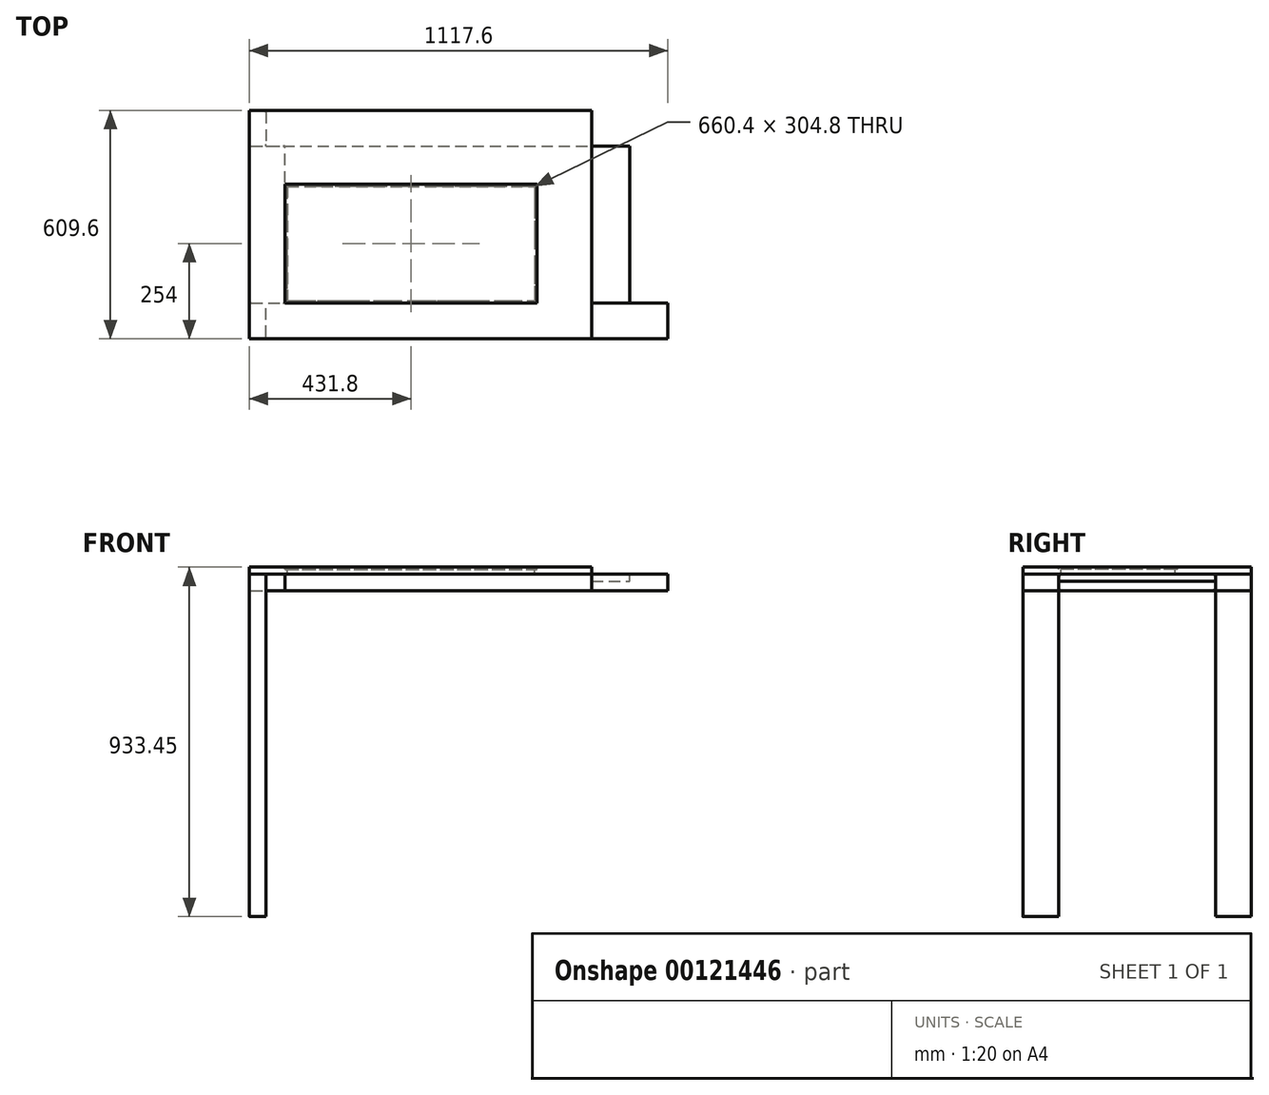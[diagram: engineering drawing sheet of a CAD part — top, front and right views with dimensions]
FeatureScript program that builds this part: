
annotation { "Feature Type Name" : "Feature", "Feature Type Description" : "" }
export const myFeature = defineFeature(function(context is Context, id is Id, definition is map)
    precondition{}
    {
        {
            var Q0;
            Q0=qCreatedBy(makeId("Top.planeOp"),FACE);
            var sketch = newSketch(context, id + "F0", { "sketchPlane" : qUnion([Q0])});
            skLineSegment(sketch, "E0.bottom", {"start": v(457.2, 304.8) * mm, "end": v(-457.2, 304.8) * mm});
            skLineSegment(sketch, "E0.top", {"start": v(457.2, -304.8) * mm, "end": v(-457.2, -304.8) * mm});
            skLineSegment(sketch, "E0.left", {"start": v(457.2, 304.8) * mm, "end": v(457.2, -304.8) * mm});
            skLineSegment(sketch, "E0.right", {"start": v(-457.2, 304.8) * mm, "end": v(-457.2, -304.8) * mm});
            skPoint(sketch, "E0.middle", {"position": v(0, 0) * mm});
            skSolve(sketch);
        }
        {
            var Q0;
            Q0 = qSketchRegion(id + "F0", true);
            extrude(context, id + "F1", {"entities" : qUnion([Q0]), "depth" : 19.05 * mm});
        }
        {
            var Q0;
            Q0=makeQuery(id+"F1.opExtrude","CAP_FACE",FACE,{"disambiguationData":[OSD([sQuery(id+"F0.wireOp",EDGE,"E0.bottom"),sQuery(id+"F0.wireOp",EDGE,"E0.top"),sQuery(id+"F0.wireOp",EDGE,"E0.left"),sQuery(id+"F0.wireOp",EDGE,"E0.right")])],"isStart":true});
            var sketch = newSketch(context, id + "F2", { "sketchPlane" : qUnion([Q0])});
            skLineSegment(sketch, "E1.bottom", {"start": v(-457.2, 304.8) * mm, "end": v(-412.75, 304.8) * mm});
            skLineSegment(sketch, "E1.top", {"start": v(-457.2, 209.55) * mm, "end": v(-412.75, 209.55) * mm});
            skLineSegment(sketch, "E1.left", {"start": v(-457.2, 304.8) * mm, "end": v(-457.2, 209.55) * mm});
            skLineSegment(sketch, "E1.right", {"start": v(-412.75, 304.8) * mm, "end": v(-412.75, 209.55) * mm});
            skLineSegment(sketch, "E2.bottom", {"start": v(-457.2, -304.8) * mm, "end": v(-412.75, -304.8) * mm});
            skLineSegment(sketch, "E2.top", {"start": v(-457.2, -209.55) * mm, "end": v(-412.75, -209.55) * mm});
            skLineSegment(sketch, "E2.left", {"start": v(-457.2, -304.8) * mm, "end": v(-457.2, -209.55) * mm});
            skLineSegment(sketch, "E2.right", {"start": v(-412.75, -304.8) * mm, "end": v(-412.75, -209.55) * mm});
            skLineSegment(sketch, "E3.bottom", {"start": v(-412.75, -209.55) * mm, "end": v(457.2, -209.55) * mm});
            skLineSegment(sketch, "E3.top", {"start": v(-412.75, -304.8) * mm, "end": v(457.2, -304.8) * mm});
            skLineSegment(sketch, "E3.left", {"start": v(-412.75, -209.55) * mm, "end": v(-412.75, -304.8) * mm});
            skLineSegment(sketch, "E3.right", {"start": v(457.2, -209.55) * mm, "end": v(457.2, -304.8) * mm});
            skLineSegment(sketch, "E4.bottom", {"start": v(-412.75, 209.55) * mm, "end": v(660.4, 209.55) * mm});
            skLineSegment(sketch, "E4.top", {"start": v(-412.75, 304.8) * mm, "end": v(660.4, 304.8) * mm});
            skLineSegment(sketch, "E4.left", {"start": v(-412.75, 209.55) * mm, "end": v(-412.75, 304.8) * mm});
            skLineSegment(sketch, "E4.right", {"start": v(660.4, 209.55) * mm, "end": v(660.4, 304.8) * mm});
            skLineSegment(sketch, "E5.bottom", {"start": v(-457.2, 209.55) * mm, "end": v(-361.95, 209.55) * mm});
            skLineSegment(sketch, "E5.top", {"start": v(-457.2, -209.55) * mm, "end": v(-361.95, -209.55) * mm});
            skLineSegment(sketch, "E5.left", {"start": v(-457.2, 209.55) * mm, "end": v(-457.2, -209.55) * mm});
            skLineSegment(sketch, "E5.right", {"start": v(-361.95, 209.55) * mm, "end": v(-361.95, -209.55) * mm});
            skLineSegment(sketch, "E6.bottom", {"start": v(355.6, -209.55) * mm, "end": v(558.8, -209.55) * mm});
            skLineSegment(sketch, "E6.top", {"start": v(355.6, 209.55) * mm, "end": v(558.8, 209.55) * mm});
            skLineSegment(sketch, "E6.left", {"start": v(355.6, -209.55) * mm, "end": v(355.6, 209.55) * mm});
            skLineSegment(sketch, "E6.right", {"start": v(558.8, -209.55) * mm, "end": v(558.8, 209.55) * mm});
            skSolve(sketch);
        }
        {
            var Q0;
            {var subQ3=sQuery(id+"F2.wireOp",EDGE,"E4.left");Q0=makeQuery(id+"F2.imprint","IMPRINT",FACE,{"disambiguationData":[TD([[makeQuery(id+"F2.imprint","IMPRINT",EDGE,{"derivedFrom":subQ3}),-1.0]])]});}
            var Q1;
            {var subQ1=sQuery(id+"F2.wireOp",EDGE,"E3.bottom");Q1=makeQuery(id+"F2.imprint","IMPRINT",FACE,{"disambiguationData":[TD([[makeQuery(id+"F2.imprint","IMPRINT",EDGE,{"derivedFrom":subQ1}),-1.0]])]});}
            var Q2;
            {var subQ0=sQuery(id+"F2.wireOp",EDGE,"E4.right");Q2=makeQuery(id+"F2.imprint","IMPRINT",FACE,{"disambiguationData":[TD([[makeQuery(id+"F2.imprint","IMPRINT",EDGE,{"derivedFrom":subQ0}),1.0]])]});}
            extrude(context, id + "F3", {"entities" : qUnion([Q0, Q1, Q2]), "depth" : 44.45 * mm});
        }
        {
            var Q0;
            {var subQ5=sQuery(id+"F2.wireOp",EDGE,"E5.left");Q0=makeQuery(id+"F2.imprint","IMPRINT",FACE,{"disambiguationData":[TD([[makeQuery(id+"F2.imprint","IMPRINT",EDGE,{"derivedFrom":subQ5}),-1.0]])]});}
            extrude(context, id + "F4", {"entities" : qUnion([Q0]), "depth" : 44.45 * mm});
        }
        {
            var Q0;
            Q0=makeQuery(id+"F2.imprint","IMPRINT",FACE,{"disambiguationData":[TD([[makeQuery(id+"F2.imprint","IMPRINT",EDGE,{"derivedFrom":sQuery(id+"F2.wireOp",EDGE,"E6.bottom")}),1.0]])]});
            extrude(context, id + "F5", {"entities" : qUnion([Q0]), "depth" : 19.05 * mm});
        }
        {
            var Q0;
            Q0=makeQuery(id+"F2.imprint","IMPRINT",FACE,{"disambiguationData":[TD([[makeQuery(id+"F2.imprint","IMPRINT",EDGE,{"derivedFrom":sQuery(id+"F2.wireOp",EDGE,"E1.bottom")}),1.0]])]});
            var Q1;
            Q1=makeQuery(id+"F2.imprint","IMPRINT",FACE,{"disambiguationData":[TD([[makeQuery(id+"F2.imprint","IMPRINT",EDGE,{"derivedFrom":sQuery(id+"F2.wireOp",EDGE,"E2.bottom")}),-1.0]])]});
            extrude(context, id + "F6", {"entities" : qUnion([Q0, Q1]), "depth" : 914.4 * mm});
        }
        {
            var Q0;
            Q0=makeQuery(id+"F6.opExtrude","SWEPT_EDGE",EDGE,{"disambiguationData":[OSD([sQuery(id+"F2.wireOp",EDGE,"E1.left"),sQuery(id+"F2.wireOp",EDGE,"E5.bottom"),sQuery(id+"F2.wireOp",EDGE,"E5.left")])]});
            var Q1;
            Q1=makeQuery(id+"F6.opExtrude","SWEPT_EDGE",EDGE,{"disambiguationData":[OSD([sQuery(id+"F2.wireOp",EDGE,"E4.left"),sQuery(id+"F2.wireOp",EDGE,"E5.bottom")])]});
            var Q2;
            Q2=makeQuery(id+"F6.opExtrude","SWEPT_EDGE",EDGE,{"disambiguationData":[OSD([sQuery(id+"F2.wireOp",EDGE,"E1.bottom"),sQuery(id+"F2.wireOp",EDGE,"E4.top"),sQuery(id+"F2.wireOp",EDGE,"E4.left")])]});
            var Q3;
            Q3=makeQuery(id+"F3.opExtrude","CAP_EDGE",EDGE,{"disambiguationData":[OSD([sQuery(id+"F2.wireOp",EDGE,"E4.top")])],"isStart":false});
            var Q4;
            Q4=makeQuery(id+"F3.opExtrude","CAP_EDGE",EDGE,{"disambiguationData":[OSD([sQuery(id+"F2.wireOp",EDGE,"E4.bottom"),sQuery(id+"F2.wireOp",EDGE,"E5.bottom")])],"isStart":false});
            var Q5;
            Q5=makeQuery(id+"F3.opExtrude","CAP_EDGE",EDGE,{"disambiguationData":[OSD([sQuery(id+"F2.wireOp",EDGE,"E4.bottom"),sQuery(id+"F2.wireOp",EDGE,"E5.bottom")])],"isStart":true});
            var Q6;
            Q6=makeQuery(id+"F4.opExtrude","CAP_EDGE",EDGE,{"disambiguationData":[OSD([sQuery(id+"F2.wireOp",EDGE,"E5.left")])],"isStart":false});
            var Q7;
            Q7=makeQuery(id+"F4.opExtrude","CAP_EDGE",EDGE,{"disambiguationData":[OSD([sQuery(id+"F2.wireOp",EDGE,"E5.right")])],"isStart":false});
            var Q8;
            Q8=makeQuery(id+"F4.opExtrude","CAP_EDGE",EDGE,{"disambiguationData":[OSD([sQuery(id+"F2.wireOp",EDGE,"E5.right")])],"isStart":true});
            var Q9;
            Q9=makeQuery(id+"F3.opExtrude","CAP_EDGE",EDGE,{"disambiguationData":[OSD([sQuery(id+"F2.wireOp",EDGE,"E3.top")])],"isStart":true});
            var Q10;
            Q10=makeQuery(id+"F3.opExtrude","CAP_EDGE",EDGE,{"disambiguationData":[OSD([sQuery(id+"F2.wireOp",EDGE,"E3.top")])],"isStart":false});
            var Q11;
            Q11=makeQuery(id+"F3.opExtrude","CAP_EDGE",EDGE,{"disambiguationData":[OSD([sQuery(id+"F2.wireOp",EDGE,"E3.bottom"),sQuery(id+"F2.wireOp",EDGE,"E5.top"),sQuery(id+"F2.wireOp",EDGE,"E6.bottom"),sQuery(id+"F2.wireOp",EDGE,"GO6ybiZl-LZOK-cMtS-mfAd-nQg24DWnIChV")])],"isStart":false});
            var Q12;
            Q12=makeQuery(id+"F6.opExtrude","SWEPT_EDGE",EDGE,{"disambiguationData":[OSD([sQuery(id+"F2.wireOp",EDGE,"E2.bottom"),sQuery(id+"F2.wireOp",EDGE,"E2.left")])]});
            var Q13;
            Q13=makeQuery(id+"F6.opExtrude","SWEPT_EDGE",EDGE,{"disambiguationData":[OSD([sQuery(id+"F2.wireOp",EDGE,"E2.bottom"),sQuery(id+"F2.wireOp",EDGE,"E3.top"),sQuery(id+"F2.wireOp",EDGE,"E3.left")])]});
            var Q14;
            Q14=makeQuery(id+"F6.opExtrude","SWEPT_EDGE",EDGE,{"disambiguationData":[OSD([sQuery(id+"F2.wireOp",EDGE,"E2.left"),sQuery(id+"F2.wireOp",EDGE,"E5.top"),sQuery(id+"F2.wireOp",EDGE,"E5.left")])]});
            var Q15;
            Q15=makeQuery(id+"F6.opExtrude","SWEPT_EDGE",EDGE,{"disambiguationData":[OSD([sQuery(id+"F2.wireOp",EDGE,"E1.bottom"),sQuery(id+"F2.wireOp",EDGE,"E1.left")])]});
            var Q16;
            Q16=makeQuery(id+"F3.opExtrude","CAP_EDGE",EDGE,{"disambiguationData":[OSD([sQuery(id+"F2.wireOp",EDGE,"E3.bottom"),sQuery(id+"F2.wireOp",EDGE,"E5.top"),sQuery(id+"F2.wireOp",EDGE,"E6.bottom"),sQuery(id+"F2.wireOp",EDGE,"GO6ybiZl-LZOK-cMtS-mfAd-nQg24DWnIChV")])],"isStart":true});
            var Q17;
            Q17=makeQuery(id+"F4.opExtrude","SWEPT_FACE",FACE,{"disambiguationData":[OSD([sQuery(id+"F2.wireOp",EDGE,"E5.left")])]});
            var Q18;
            Q18=makeQuery(id+"F3.opExtrude","CAP_EDGE",EDGE,{"disambiguationData":[OSD([sQuery(id+"F2.wireOp",EDGE,"E4.top")])],"isStart":true});
            var Q19;
            Q19=makeQuery(id+"F6.opExtrude","SWEPT_EDGE",EDGE,{"disambiguationData":[OSD([sQuery(id+"F2.wireOp",EDGE,"E3.left"),sQuery(id+"F2.wireOp",EDGE,"E5.top")])]});
            fillet(context, id + "F7", {"entities" : qUnion([Q0, Q1, Q2, Q3, Q4, Q5, Q6, Q7, Q8, Q9, Q10, Q11, Q12, Q13, Q14, Q15, Q16, Q17, Q18, Q19]), "radius" : 5.08 * mm, "tangentPropagation" : true, "allowEdgeOverflow" : false});
        }
        {
            var Q0;
            Q0=makeQuery(id+"F1.opExtrude","CAP_FACE",FACE,{"disambiguationData":[OSD([sQuery(id+"F0.wireOp",EDGE,"E0.bottom"),sQuery(id+"F0.wireOp",EDGE,"E0.top"),sQuery(id+"F0.wireOp",EDGE,"E0.left"),sQuery(id+"F0.wireOp",EDGE,"E0.right")])],"isStart":false});
            var sketch = newSketch(context, id + "F8", { "sketchPlane" : qUnion([Q0])});
            skLineSegment(sketch, "E7.bottom", {"start": v(-355.6, 101.6) * mm, "end": v(304.8, 101.6) * mm});
            skLineSegment(sketch, "E7.top", {"start": v(-355.6, -203.2) * mm, "end": v(304.8, -203.2) * mm});
            skLineSegment(sketch, "E7.left", {"start": v(-355.6, 101.6) * mm, "end": v(-355.6, -203.2) * mm});
            skLineSegment(sketch, "E7.right", {"start": v(304.8, 101.6) * mm, "end": v(304.8, -203.2) * mm});
            skLineSegment(sketch, "E8.bottom", {"start": v(-361.95, 107.95) * mm, "end": v(311.15, 107.95) * mm});
            skLineSegment(sketch, "E8.top", {"start": v(-361.95, -209.55) * mm, "end": v(311.15, -209.55) * mm});
            skLineSegment(sketch, "E8.left", {"start": v(-361.95, 107.95) * mm, "end": v(-361.95, -209.55) * mm});
            skLineSegment(sketch, "E8.right", {"start": v(311.15, 107.95) * mm, "end": v(311.15, -209.55) * mm});
            skLineSegment(sketch, "E9", {"start": v(-355.6, 101.6) * mm, "end": v(-355.6, 107.95) * mm, "construction": true});
            skLineSegment(sketch, "E10", {"start": v(-355.6, 101.6) * mm, "end": v(-361.95, 101.6) * mm, "construction": true});
            skLineSegment(sketch, "E11", {"start": v(304.8, -203.2) * mm, "end": v(311.15, -203.2) * mm, "construction": true});
            skLineSegment(sketch, "E12", {"start": v(304.8, -203.2) * mm, "end": v(304.8, -209.55) * mm, "construction": true});
            skSolve(sketch);
        }
        {
            var Q0;
            Q0 = qSketchRegion(id + "F8", true);
            extrude(context, id + "F9", {"entities" : qUnion([Q0]), "operationType" : NewBodyOperationType.REMOVE, "oppositeDirection" : true, "depth" : 6.35 * mm});
        }
        {
            var Q0;
            Q0=makeQuery(id+"F9.boolean.opBoolean","SPLIT",FACE,{"disambiguationData":[TD([makeQuery(id+"F9.opExtrude","SWEPT_FACE",FACE,{"disambiguationData":[OSD([sQuery(id+"F8.wireOp",EDGE,"E7.bottom")])]})])],"derivedFrom":makeQuery(id+"F1.opExtrude","CAP_FACE",FACE,{"disambiguationData":[OSD([sQuery(id+"F0.wireOp",EDGE,"E0.bottom"),sQuery(id+"F0.wireOp",EDGE,"E0.top"),sQuery(id+"F0.wireOp",EDGE,"E0.left"),sQuery(id+"F0.wireOp",EDGE,"E0.right")])],"isStart":false})});
            extrude(context, id + "F10", {"entities" : qUnion([Q0]), "operationType" : NewBodyOperationType.REMOVE, "oppositeDirection" : true, "depth" : 25.4 * mm});
        }
        {
            var Q0;
            Q0=makeQuery(id+"F8.imprint","IMPRINT",FACE,{"disambiguationData":[TD([[makeQuery(id+"F8.imprint","IMPRINT",EDGE,{"derivedFrom":sQuery(id+"F8.wireOp",EDGE,"E7.bottom")}),-1.0]])]});
            var Q1;
            Q1=makeQuery(id+"F8.imprint","IMPRINT",FACE,{"disambiguationData":[TD([[makeQuery(id+"F8.imprint","IMPRINT",EDGE,{"derivedFrom":sQuery(id+"F8.wireOp",EDGE,"E7.bottom")}),1.0]])]});
            extrude(context, id + "F11", {"entities" : qUnion([Q0, Q1]), "oppositeDirection" : true, "depth" : 6.35 * mm});
        }
    });
